# Revit family: NLRS_57_GEN_UN_roof-curb-for-bdcn_LT_sacs
name_source: partatom
category: Duct Accessories
units: mm (PartAtom-declared; Revit-internal decimal feet)

## family parameters
Always vertical = Yes
Cut with Voids When Loaded = No
Part Type = Attaches To
Round Connector Dimension = Use Diameter
Shared = Yes
Work Plane-Based = No

## types (2) — shared parameters
Assembly Code = 57.0
Manufacturer = Solid Air Climate Solutions
Model = Solid Air roof curb, BDOC for BDCN
NLRS_C_content_datum_uitgifte = 21-07-2025
NLRS_C_content_provider = Solid Air Climate Solutions
NLRS_C_content_versie = 1.22.01
SACS_Data_Hidden = BDOCA
SACS_Material = Seawater proof aluminium
Type Comments = SACS_Length = L1 + L2 +100, see penthouse BDCN
zero-valued in all types: Default Elevation

## per-type parameters (varying)
| type | Description | NLRS_C_description | SACS_Base_Index | SACS_Frame_1 | SACS_Frame_2 |
| BDOCAD | Aluminum roof curb, non-insulated | Aluminum roof curb, non-insulated | 3 | Yes | No |
| BDOCAR | Aluminum roof curb, insulated | Aluminum roof curb, insulated | 4 | No | Yes |

## geometry (parser evidence)
native form markers: Sweep x6
no freeform markers — native parametric forms only
